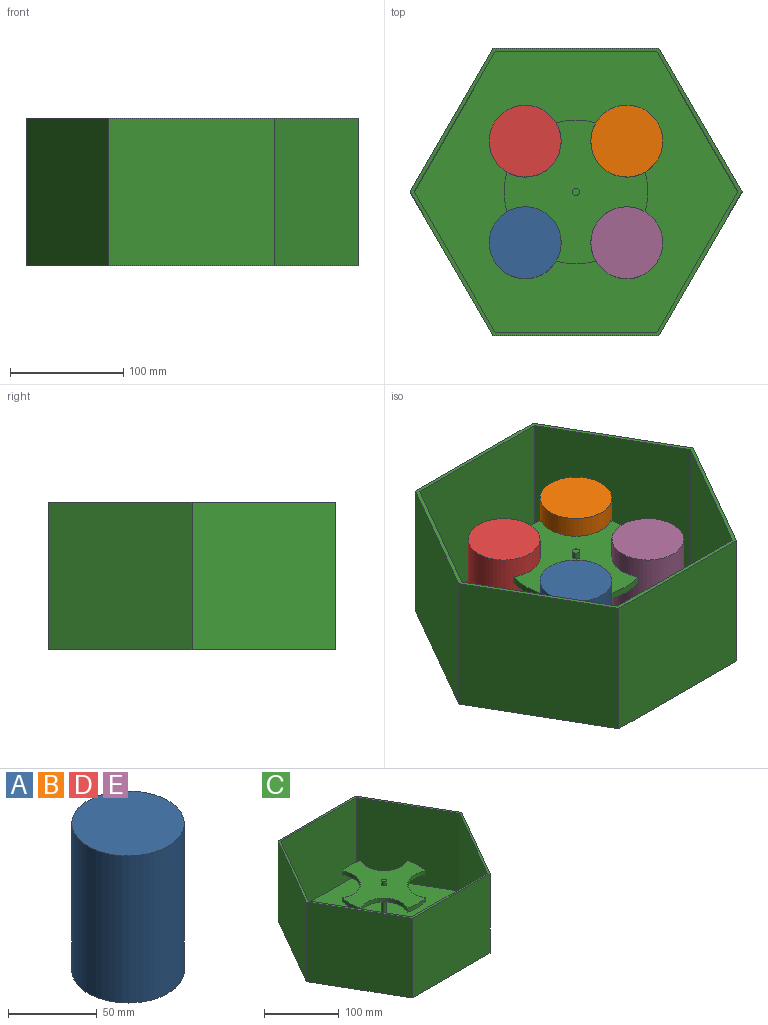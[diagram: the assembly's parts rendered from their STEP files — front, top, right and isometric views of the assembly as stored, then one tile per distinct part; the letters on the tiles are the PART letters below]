
ASSEMBLY  parts=5 mates=2
PART A: 3 faces, bbox 63.5x63.5x101.6 mm
  f0: cylinder r=31.75mm len=101.6mm, axis (0,0,-1), area 20268.3mm2, adj f1,f2
  f1: plane 63.5x63.5mm, normal (0,0,1), area 3166.9mm2, adj f0
  f2: plane 63.5x63.5mm, normal (0,0,-1), area 3166.9mm2, adj f0
PART B: same geometry as A
PART C: 28 faces, bbox 293.3x254x130.2 mm
  f0: cylinder r=63.5mm len=35.1mm, axis (0,0,-1), area 225.8mm2, adj f20,f21,f26,f27
  f1: cylinder r=63.5mm len=35.1mm, axis (0,0,-1), area 225.8mm2, adj f20,f21,f25,f26
  f2: cylinder r=63.5mm len=35.1mm, axis (0,0,-1), area 225.8mm2, adj f20,f21,f24,f25
  f3: cylinder r=3.17mm len=76.2mm, axis (0,0,-1), area 1520.1mm2, adj f18,f21
  f4: plane 146.65x130.18mm, normal (0,-1,0), area 19089.8mm2, adj f5,f9,f10,f17
  f5: plane 130.18x127mm, normal (0.87,-0.5,0), area 19089.8mm2, adj f4,f6,f10,f17
  f6: plane 130.18x127mm, normal (0.87,0.5,0), area 19089.8mm2, adj f5,f7,f10,f17
  f7: plane 146.65x130.18mm, normal (0,1,0), area 19089.8mm2, adj f6,f8,f10,f17
  f8: plane 130.18x127mm, normal (-0.87,0.5,0), area 19089.8mm2, adj f7,f9,f10,f17
  f9: plane 130.18x127mm, normal (-0.87,-0.5,0), area 19089.8mm2, adj f4,f8,f10,f17
  f10: plane 293.29x254mm, normal (0,0,-1), area 55872.5mm2, adj f4,f5,f6,f7,f8,f9
  f11: plane 127x123.83mm, normal (0.87,-0.5,0), area 18158.6mm2, adj f12,f16,f17,f18
  f12: plane 142.98x127mm, normal (0,-1,0), area 18158.6mm2, adj f11,f13,f17,f18
  f13: plane 127x123.83mm, normal (-0.87,-0.5,0), area 18158.6mm2, adj f12,f14,f17,f18
  f14: plane 127x123.83mm, normal (-0.87,0.5,0), area 18158.6mm2, adj f13,f15,f17,f18
  f15: plane 142.98x127mm, normal (0,1,0), area 18158.6mm2, adj f14,f16,f17,f18
  f16: plane 127x123.83mm, normal (0.87,0.5,0), area 18158.6mm2, adj f11,f15,f17,f18
  f17: plane 293.29x254mm, normal (0,0,1), area 2758.7mm2, adj f4,f5,f6,f7,f8,f9,f11,f12
  f18: plane 285.96x247.65mm, normal (0,0,1), area 53082.1mm2, adj f3,f11,f12,f13,f14,f15,f16
  f19: cylinder r=63.5mm len=35.1mm, axis (0,0,-1), area 225.8mm2, adj f20,f21,f24,f27
  f20: plane 127x127mm, normal (0,0,1), area 6978.5mm2, adj f0,f1,f2,f19,f23,f24,f25,f26
  f21: plane 127x127mm, normal (0,0,-1), area 6978.5mm2, adj f0,f1,f2,f3,f19,f24,f25,f26
  f22: plane 6.35x6.35mm, normal (0,0,1), area 31.7mm2, adj f23
  f23: cylinder r=3.17mm len=6.35mm, axis (0,0,-1), area 126.7mm2, adj f20,f22
  f24: cylinder r=31.75mm len=47.88mm, axis (0,0,1), area 531.5mm2, adj f2,f19,f20,f21
  f25: cylinder r=31.75mm len=47.88mm, axis (0,0,1), area 531.5mm2, adj f1,f2,f20,f21
  f26: cylinder r=31.75mm len=47.88mm, axis (0,0,1), area 531.5mm2, adj f0,f1,f20,f21
  f27: cylinder r=31.75mm len=47.88mm, axis (0,0,1), area 531.5mm2, adj f0,f19,f20,f21
PART D: same geometry as A
PART E: same geometry as A
PLACE A t=(-44.9,-44.9,-100.01)mm
PLACE B rot(axis=(0,0,1),180deg) t=(44.9,44.9,-100.01)mm
PLACE C t=(0,0,-103.19)mm fixed
PLACE D rot(axis=(0,0,-1),90deg) t=(-44.9,44.9,-100.01)mm
PLACE E rot(axis=(0,0,1),90deg) t=(44.9,-44.9,-100.01)mm
MATE cylindrical C.f25 <-> D.f0  axis (0,0,1) through (-44.9,44.9,-17.46)mm
MATE planar C.f3 <-> D.f0  axis (0,0,1) through (0,0,-100.01)mm
